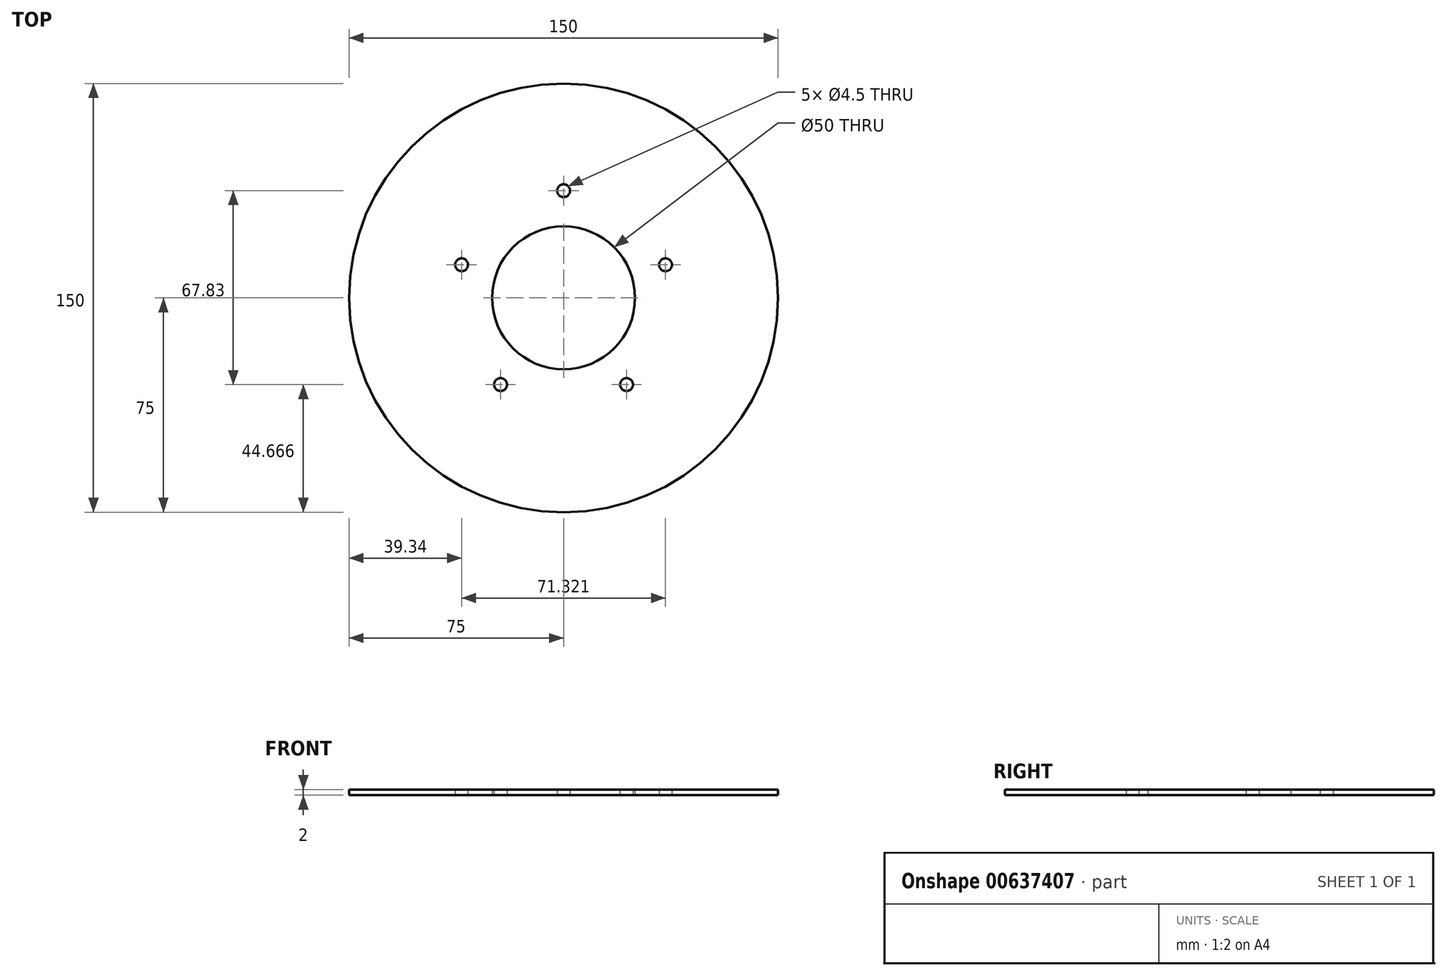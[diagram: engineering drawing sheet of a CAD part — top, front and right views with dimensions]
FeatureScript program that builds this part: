
annotation { "Feature Type Name" : "Feature", "Feature Type Description" : "" }
export const myFeature = defineFeature(function(context is Context, id is Id, definition is map)
    precondition{}
    {
        {
            var Q0;
            Q0=qCreatedBy(makeId("Top.planeOp"),FACE);
            var sketch = newSketch(context, id + "F0", { "sketchPlane" : qUnion([Q0])});
            skCircle(sketch, "E0", {"center": v(0, 0) * mm, "radius": 75 * mm});
            skCircle(sketch, "E1", {"center": v(0, 0) * mm, "radius": 25 * mm});
            skCircle(sketch, "E2", {"center": v(0, 37.5) * mm, "radius": 2.25 * mm});
            skCircle(sketch, "E3.1.0", {"center": v(-35.66, 11.59) * mm, "radius": 2.25 * mm});
            skCircle(sketch, "E3.2.0", {"center": v(-22.04, -30.33) * mm, "radius": 2.25 * mm});
            skCircle(sketch, "E3.3.0", {"center": v(22.04, -30.33) * mm, "radius": 2.25 * mm});
            skCircle(sketch, "E3.4.0", {"center": v(35.66, 11.59) * mm, "radius": 2.25 * mm});
            skSolve(sketch);
        }
        {
            var Q0;
            Q0=makeQuery(id+"F0.imprint","IMPRINT",FACE,{"disambiguationData":[TD([[makeQuery(id+"F0.imprint","IMPRINT",EDGE,{"derivedFrom":sQuery(id+"F0.wireOp",EDGE,"E0")}),1.0]])]});
            extrude(context, id + "F1", {"entities" : qUnion([Q0]), "depth" : 2 * mm, "offsetDistance" : 25 * mm});
        }
    });
